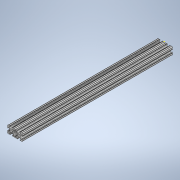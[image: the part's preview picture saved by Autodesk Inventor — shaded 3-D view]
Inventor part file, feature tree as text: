
AUTODESK INVENTOR PART (.ipt)
format: ipt  version: 2020 (Build 240168000, 168)  size: 332,800 bytes
history: native  units: in
note: dims shown in document units (in); Inventor stores cm internally (conversion verified against a paired STEP export)
features: sketch x2, extrude x1
ambient origin geometry x8: Origin, YZ Plane, XZ Plane, XY Plane, X Axis, Y Axis, Z Axis, Center Point
bodies: Solid1 (feature_tree)
feature tree (3):
  extrude  "Extrusion1"  [1 undecoded]
  sketch  "Sketch2"
  sketch  "Sketch1"  dims[d0=20.0in d1=0.0in]
note: 1 required parameter value undecoded (feature->parameter linkage not recoverable at this tier; creation-order binding heuristic only, values carry confidence <= 0.55)
